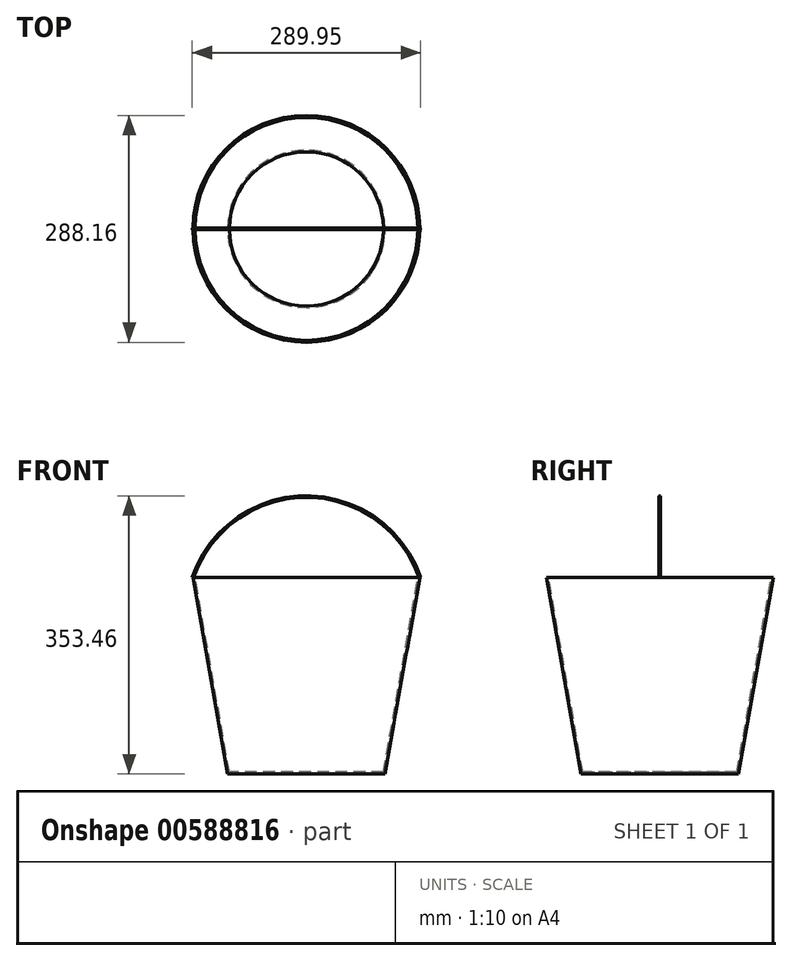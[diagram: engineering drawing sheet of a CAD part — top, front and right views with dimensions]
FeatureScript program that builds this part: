
annotation { "Feature Type Name" : "Feature", "Feature Type Description" : "" }
export const myFeature = defineFeature(function(context is Context, id is Id, definition is map)
    precondition{}
    {
        {
            var Q0;
            Q0=qCreatedBy(makeId("Top.planeOp"),FACE);
            var sketch = newSketch(context, id + "F0", { "sketchPlane" : qUnion([Q0])});
            skCircle(sketch, "E0", {"center": v(0, 0) * mm, "radius": 100 * mm});
            skSolve(sketch);
        }
        {
            var Q0;
            Q0=makeQuery(id+"F0.imprint","IMPRINT",FACE,{"disambiguationData":[TD([[makeQuery(id+"F0.imprint","IMPRINT",EDGE,{"derivedFrom":sQuery(id+"F0.wireOp",EDGE,"E0")}),1.0]])]});
            extrude(context, id + "F1", {"entities" : qUnion([Q0]), "depth" : 250 * mm, "offsetDistance" : 25 * mm, "hasDraft" : true, "draftAngle" : 10 * degree});
        }
        {
            var Q0;
            Q0=makeQuery(id+"F1.opExtrude","CAP_FACE",FACE,{"disambiguationData":[OSD([sQuery(id+"F0.wireOp",EDGE,"E0")])],"isStart":false});
            shell(context, id + "F2", {"entities" : qUnion([Q0]), "thickness" : 2.5 * mm});
        }
        {
            var Q0;
            Q0=qCreatedBy(makeId("Front.planeOp"),FACE);
            var sketch = newSketch(context, id + "F3", { "sketchPlane" : qUnion([Q0])});
            skArc(sketch, "E1", {"start": v(144.08, 250) * mm, "mid": v(0, 352.51) * mm, "end": v(-144.08, 250) * mm});
            skSolve(sketch);
        }
        {
            var Q0;
            Q0=qCreatedBy(makeId("Top.planeOp"),FACE);
            cPlane(context, id + "F4", {"entities" : qUnion([Q0]), "cplaneType" : CPlaneType.OFFSET, "offset" : 250 * mm, "width" : 150 * mm, "height" : 150 * mm});
        }
        {
            var Q0;
            Q0=qCreatedBy(id+"F4.planeOp",FACE);
            var sketch = newSketch(context, id + "F5", { "sketchPlane" : qUnion([Q0])});
            skCircle(sketch, "E2", {"center": v(-144.08, 0) * mm, "radius": 1 * mm});
            skSolve(sketch);
        }
        {
            var Q0;
            Q0=makeQuery(id+"F5.imprint","IMPRINT",FACE,{"disambiguationData":[TD([[makeQuery(id+"F5.imprint","IMPRINT",EDGE,{"derivedFrom":sQuery(id+"F5.wireOp",EDGE,"E2")}),1.0]])]});
            var Q1;
            Q1=sQuery(id+"F3.wireOp",EDGE,"E1");
            sweep(context, id + "F6", {"operationType" : NewBodyOperationType.ADD, "profiles" : qUnion([Q0]), "path" : qUnion([Q1])});
        }
    });
